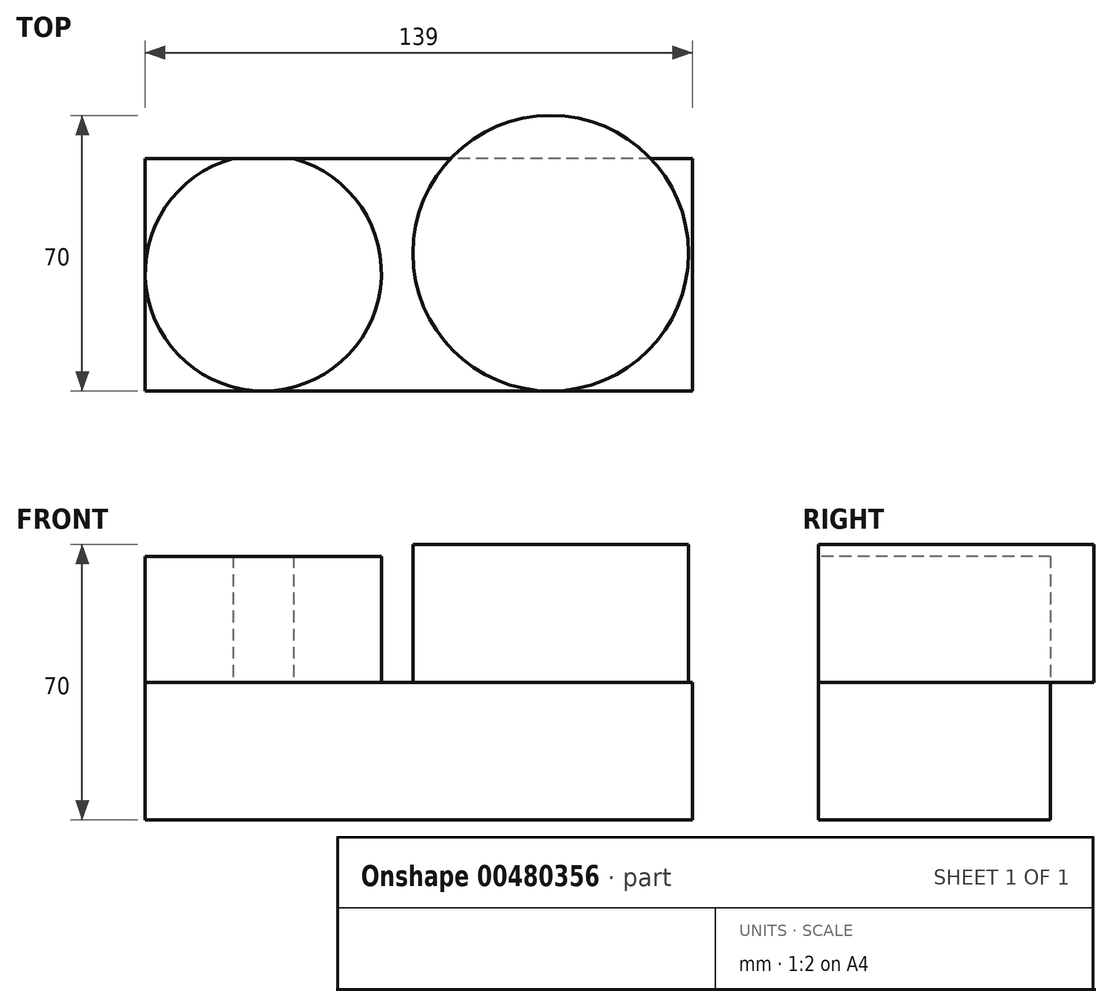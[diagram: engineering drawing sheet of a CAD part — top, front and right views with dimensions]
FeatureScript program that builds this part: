
annotation { "Feature Type Name" : "Feature", "Feature Type Description" : "" }
export const myFeature = defineFeature(function(context is Context, id is Id, definition is map)
    precondition{}
    {
        {
            var Q0;
            Q0=qCreatedBy(makeId("Top.planeOp"),FACE);
            var sketch = newSketch(context, id + "F0", { "sketchPlane" : qUnion([Q0])});
            skLineSegment(sketch, "E0.bottom", {"start": v(69.5, -29.5) * mm, "end": v(-69.5, -29.5) * mm});
            skLineSegment(sketch, "E0.top", {"start": v(69.5, 29.5) * mm, "end": v(-69.5, 29.5) * mm});
            skLineSegment(sketch, "E0.left", {"start": v(69.5, -29.5) * mm, "end": v(69.5, 29.5) * mm});
            skLineSegment(sketch, "E0.right", {"start": v(-69.5, -29.5) * mm, "end": v(-69.5, 29.5) * mm});
            skPoint(sketch, "E0.middle", {"position": v(0, 0) * mm});
            skCircle(sketch, "E1", {"center": v(-39.5, 0.5) * mm, "radius": 30 * mm});
            skCircle(sketch, "E2", {"center": v(33.5, 5.5) * mm, "radius": 35 * mm});
            skLineSegment(sketch, "E3.bottom", {"start": v(70.5, -31.5) * mm, "end": v(-71.5, -31.5) * mm, "construction": true});
            skLineSegment(sketch, "E3.top", {"start": v(70.5, 41.5) * mm, "end": v(-71.5, 41.5) * mm, "construction": true});
            skLineSegment(sketch, "E3.left", {"start": v(70.5, -31.5) * mm, "end": v(70.5, 41.5) * mm, "construction": true});
            skLineSegment(sketch, "E3.right", {"start": v(-71.5, -31.5) * mm, "end": v(-71.5, 41.5) * mm, "construction": true});
            skSolve(sketch);
        }
        {
            var Q0;
            Q0=makeQuery(id+"F0.imprint","IMPRINT",FACE,{"disambiguationData":[TD([[makeQuery(id+"F0.imprint","IMPRINT",EDGE,{"derivedFrom":sQuery(id+"F0.wireOp",EDGE,"E2")}),1.0]])]});
            var Q1;
            {var subQ0=sQuery(id+"F0.wireOp",EDGE,"E2");var subQ1=sQuery(id+"F0.wireOp",EDGE,"E0.top");var subQ2=makeQuery(id+"F0.imprint","INTERSECT",VERTEX,{"disambiguationData":[OD(0.0)],"derivedFrom":[subQ1,subQ0]});Q1=makeQuery(id+"F0.imprint","IMPRINT",FACE,{"disambiguationData":[TD([[makeQuery(id+"F0.imprint","IMPRINT",EDGE,{"disambiguationData":[TD([[subQ2,-1.0]])],"derivedFrom":subQ1}),-1.0]])]});}
            extrude(context, id + "F1", {"entities" : qUnion([Q0, Q1]), "depth" : 35 * mm});
        }
        {
            var Q0;
            Q0=makeQuery(id+"F0.imprint","IMPRINT",FACE,{"disambiguationData":[TD([[makeQuery(id+"F0.imprint","IMPRINT",EDGE,{"derivedFrom":sQuery(id+"F0.wireOp",EDGE,"E1")}),1.0]])]});
            extrude(context, id + "F2", {"entities" : qUnion([Q0]), "depth" : 32 * mm});
        }
        {
            var Q0;
            {var subQ0=sQuery(id+"F0.wireOp",EDGE,"E0.right");Q0=makeQuery(id+"F0.imprint","IMPRINT",FACE,{"disambiguationData":[TD([[makeQuery(id+"F0.imprint","IMPRINT",EDGE,{"derivedFrom":subQ0}),-1.0]])]});}
            var Q1;
            {var subQ0=sQuery(id+"F0.wireOp",EDGE,"E1");var subQ1=sQuery(id+"F0.wireOp",EDGE,"E0.top");var subQ2=makeQuery(id+"F0.imprint","INTERSECT",VERTEX,{"disambiguationData":[OD(0.0)],"derivedFrom":[subQ1,subQ0]});Q1=makeQuery(id+"F0.imprint","IMPRINT",FACE,{"disambiguationData":[TD([[makeQuery(id+"F0.imprint","IMPRINT",EDGE,{"disambiguationData":[TD([[subQ2,-1.0]])],"derivedFrom":subQ1}),1.0]])]});}
            var Q2;
            {var subQ0=sQuery(id+"F0.wireOp",EDGE,"E2");var subQ1=sQuery(id+"F0.wireOp",EDGE,"E0.top");var subQ2=makeQuery(id+"F0.imprint","INTERSECT",VERTEX,{"disambiguationData":[OD(0.0)],"derivedFrom":[subQ1,subQ0]});Q2=makeQuery(id+"F0.imprint","IMPRINT",FACE,{"disambiguationData":[TD([[makeQuery(id+"F0.imprint","IMPRINT",EDGE,{"disambiguationData":[TD([[subQ2,-1.0]])],"derivedFrom":subQ1}),1.0]])]});}
            var Q3;
            {var subQ0=sQuery(id+"F0.wireOp",EDGE,"E0.left");Q3=makeQuery(id+"F0.imprint","IMPRINT",FACE,{"disambiguationData":[TD([[makeQuery(id+"F0.imprint","IMPRINT",EDGE,{"derivedFrom":subQ0}),1.0]])]});}
            var Q4;
            {var subQ0=sQuery(id+"F0.wireOp",EDGE,"E2");var subQ1=sQuery(id+"F0.wireOp",EDGE,"E0.bottom");var subQ2=makeQuery(id+"F0.imprint","INTERSECT",VERTEX,{"derivedFrom":[subQ1,subQ0]});Q4=makeQuery(id+"F0.imprint","IMPRINT",FACE,{"disambiguationData":[TD([[makeQuery(id+"F0.imprint","IMPRINT",EDGE,{"disambiguationData":[TD([[subQ2,-1.0]])],"derivedFrom":subQ1}),-1.0]])]});}
            extrude(context, id + "F3", {"entities" : qUnion([Q0, Q1, Q2, Q3, Q4]), "oppositeDirection" : true, "depth" : 35 * mm});
        }
    });
